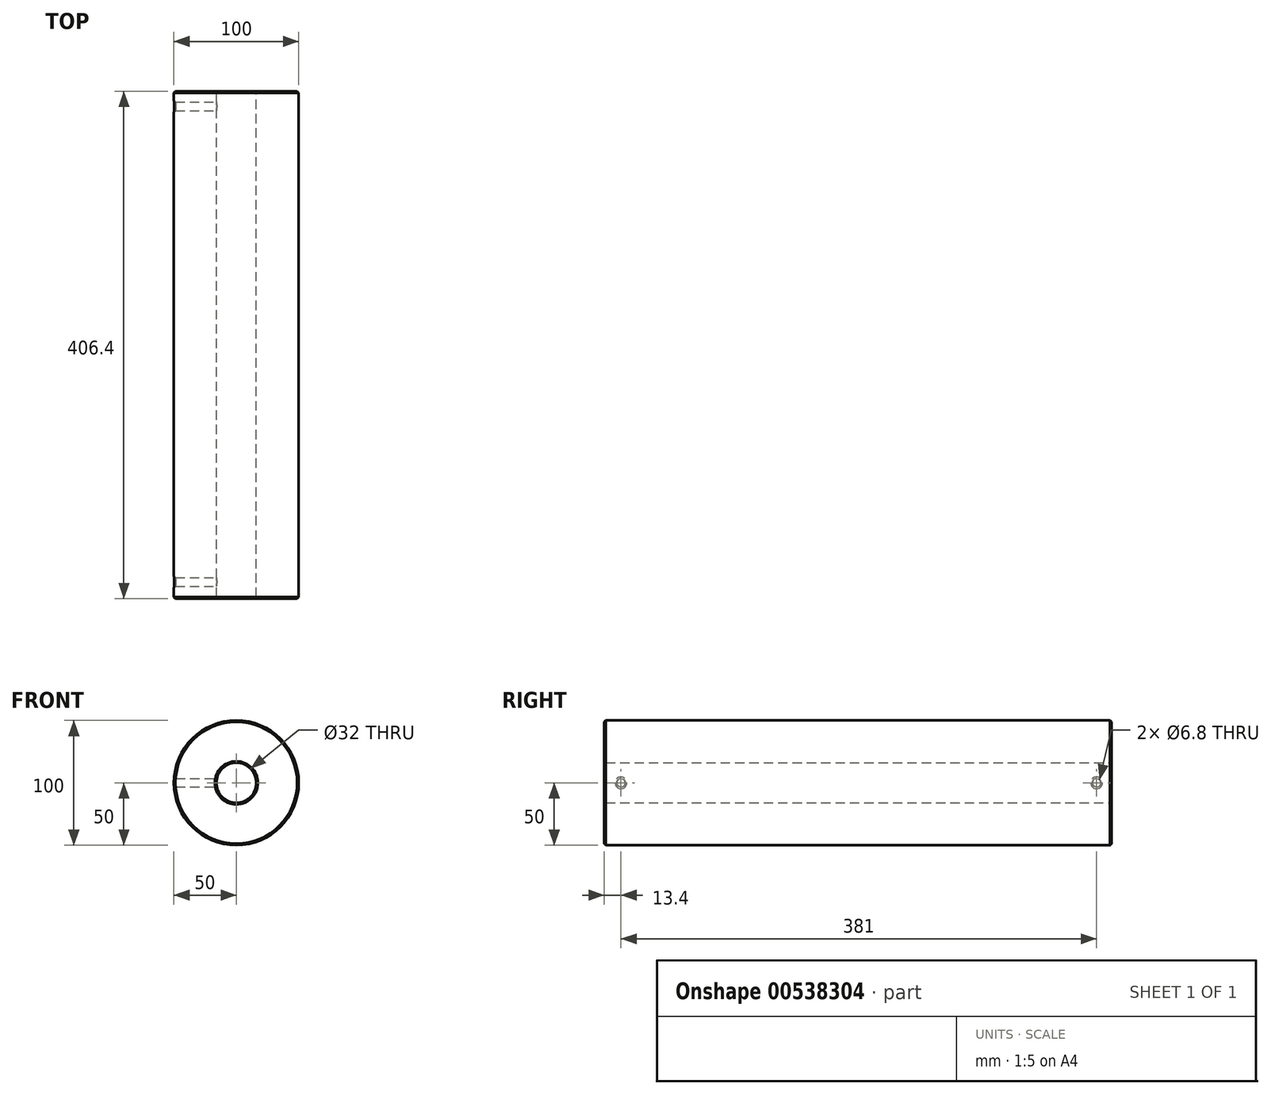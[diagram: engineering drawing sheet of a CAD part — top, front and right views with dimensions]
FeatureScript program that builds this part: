
annotation { "Feature Type Name" : "Feature", "Feature Type Description" : "" }
export const myFeature = defineFeature(function(context is Context, id is Id, definition is map)
    precondition{}
    {
        {
            var Q0;
            Q0=qCreatedBy(makeId("Front.planeOp"),FACE);
            var sketch = newSketch(context, id + "F0", { "sketchPlane" : qUnion([Q0])});
            skCircle(sketch, "E0", {"center": v(0, 0) * mm, "radius": 50 * mm});
            skCircle(sketch, "E1", {"center": v(0, 0) * mm, "radius": 16 * mm});
            skSolve(sketch);
        }
        {
            var Q0;
            Q0=makeQuery(id+"F0.imprint","IMPRINT",FACE,{"disambiguationData":[TD([[makeQuery(id+"F0.imprint","IMPRINT",EDGE,{"derivedFrom":sQuery(id+"F0.wireOp",EDGE,"E0")}),1.0]])]});
            extrude(context, id + "F1", {"entities" : qUnion([Q0]), "depth" : 406.4 * mm, "offsetDistance" : 25.4 * mm});
        }
        {
            var Q0;
            Q0=qCreatedBy(makeId("Right.planeOp"),FACE);
            var sketch = newSketch(context, id + "F2", { "sketchPlane" : qUnion([Q0])});
            skCircle(sketch, "E2", {"center": v(-12, 0) * mm, "radius": 3.4 * mm});
            skCircle(sketch, "E3", {"center": v(-393, 0) * mm, "radius": 3.4 * mm});
            skSolve(sketch);
        }
        {
            var Q0;
            Q0 = qSketchRegion(id + "F2", true);
            extrude(context, id + "F3", {"entities" : qUnion([Q0]), "operationType" : NewBodyOperationType.REMOVE, "endBound" : BoundingType.THROUGH_ALL, "oppositeDirection" : true, "depth" : 25.4 * mm, "offsetDistance" : 25.4 * mm});
        }
        {
            var Q0;
            Q0=makeQuery(id+"F1.opExtrude","CAP_EDGE",EDGE,{"disambiguationData":[OSD([sQuery(id+"F0.wireOp",EDGE,"E0")])],"isStart":false});
            var Q1;
            Q1=makeQuery(id+"F1.opExtrude","CAP_EDGE",EDGE,{"disambiguationData":[OSD([sQuery(id+"F0.wireOp",EDGE,"E1")])],"isStart":true});
            var Q2;
            Q2=makeQuery(id+"F1.opExtrude","CAP_EDGE",EDGE,{"disambiguationData":[OSD([sQuery(id+"F0.wireOp",EDGE,"E1")])],"isStart":false});
            var Q3;
            Q3=makeQuery(id+"F1.opExtrude","CAP_EDGE",EDGE,{"disambiguationData":[OSD([sQuery(id+"F0.wireOp",EDGE,"E0")])],"isStart":true});
            chamfer(context, id + "F4", {"entities" : qUnion([Q0, Q1, Q2, Q3]), "width" : 1.27 * mm, "tangentPropagation" : true});
        }
        {
            var Q0;
            Q0=makeQuery(id+"F3.boolean.opBoolean","INTERSECT",EDGE,{"derivedFrom":[makeQuery(id+"F1.opExtrude","SWEPT_FACE",FACE,{"disambiguationData":[OSD([sQuery(id+"F0.wireOp",EDGE,"E0")])]}),makeQuery(id+"F3.opExtrude","SWEPT_FACE",FACE,{"disambiguationData":[OSD([sQuery(id+"F2.wireOp",EDGE,"E2")])]})]});
            var Q1;
            Q1=makeQuery(id+"F3.boolean.opBoolean","INTERSECT",EDGE,{"derivedFrom":[makeQuery(id+"F1.opExtrude","SWEPT_FACE",FACE,{"disambiguationData":[OSD([sQuery(id+"F0.wireOp",EDGE,"E0")])]}),makeQuery(id+"F3.opExtrude","SWEPT_FACE",FACE,{"disambiguationData":[OSD([sQuery(id+"F2.wireOp",EDGE,"E3")])]})]});
            chamfer(context, id + "F5", {"entities" : qUnion([Q0, Q1]), "width" : 1.27 * mm, "tangentPropagation" : true});
        }
    });
